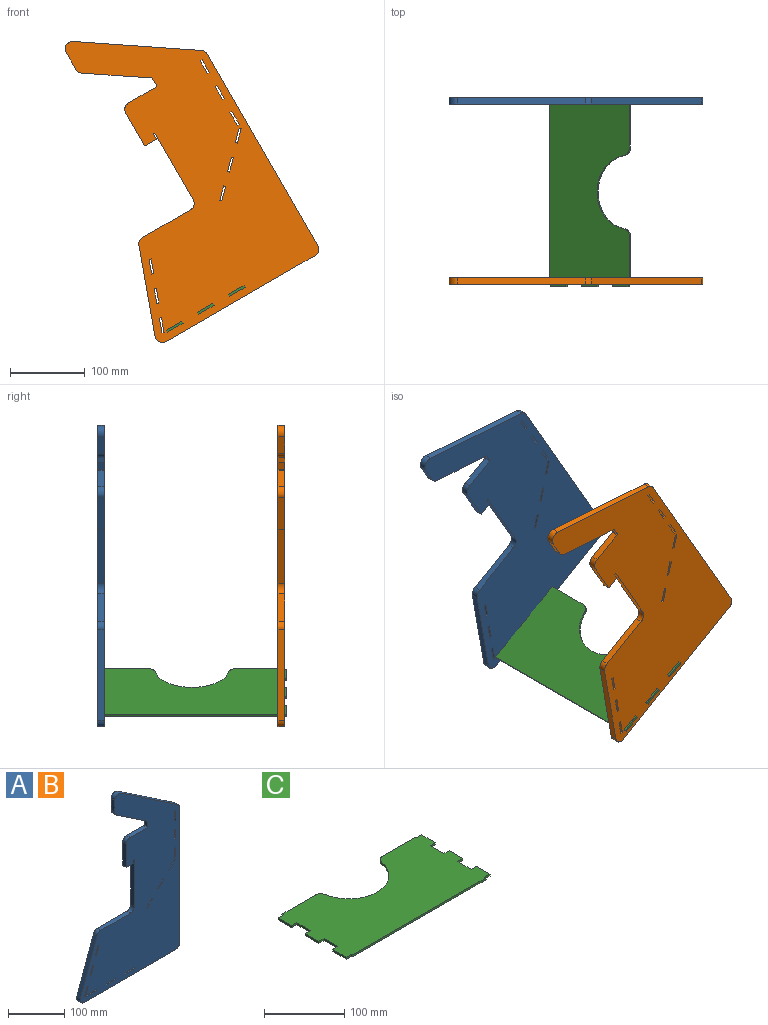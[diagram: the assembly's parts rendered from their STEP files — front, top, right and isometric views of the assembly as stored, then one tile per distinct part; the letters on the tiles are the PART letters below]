
ASSEMBLY  parts=3 mates=6
PART A: 77 faces, bbox 250.5x9x412.1 mm
  f0: plane 9x2.73mm, normal (-0.34,0,-0.94), area 26.1mm2, adj f1,f74,f75,f76
  f1: plane 18.79x9mm, normal (-0.94,0,0.34), area 180mm2, adj f0,f2,f75,f76
  f2: plane 9x2.73mm, normal (0.34,0,0.94), area 26.1mm2, adj f1,f74,f75,f76
  f3: plane 9x2.9mm, normal (1,0,0), area 26.1mm2, adj f4,f62,f75,f76
  f4: plane 24x9mm, normal (0,0,-1), area 216mm2, adj f3,f5,f75,f76
  f5: plane 9x2.9mm, normal (-1,0,0), area 26.1mm2, adj f4,f62,f75,f76
  f6: plane 9x2.9mm, normal (1,0,0), area 26.1mm2, adj f7,f63,f75,f76
  f7: plane 24x9mm, normal (0,0,-1), area 216mm2, adj f6,f8,f75,f76
  f8: plane 9x2.9mm, normal (-1,0,0), area 26.1mm2, adj f7,f63,f75,f76
  f9: plane 14.14x14.14mm, normal (0.71,0,-0.71), area 180mm2, adj f10,f64,f75,f76
  f10: plane 9x2.05mm, normal (-0.71,0,-0.71), area 26.1mm2, adj f9,f11,f75,f76
  f11: plane 14.14x14.14mm, normal (-0.71,0,0.71), area 180mm2, adj f10,f64,f75,f76
  f12: plane 9x2.9mm, normal (0,0,1), area 26.1mm2, adj f13,f65,f75,f76
  f13: plane 20x9mm, normal (1,0,0), area 180mm2, adj f12,f14,f75,f76
  f14: plane 9x2.9mm, normal (0,0,-1), area 26.1mm2, adj f13,f65,f75,f76
  f15: plane 9x2.9mm, normal (0,0,1), area 26.1mm2, adj f16,f66,f75,f76
  f16: plane 20x9mm, normal (1,0,0), area 180mm2, adj f15,f17,f75,f76
  f17: plane 9x2.9mm, normal (0,0,-1), area 26.1mm2, adj f16,f66,f75,f76
  f18: plane 16x9mm, normal (0,0,-1), area 144mm2, adj f19,f67,f75,f76
  f19: cylinder r=1mm len=9mm, axis (0,1,0), area 14.1mm2, adj f18,f20,f75,f76
  f20: plane 9x7mm, normal (1,0,0), area 63mm2, adj f19,f21,f75,f76
  f21: cylinder r=1mm len=9mm, axis (0,1,0), area 14.1mm2, adj f20,f22,f75,f76
  f22: plane 9x0.2mm, normal (0,0,-1), area 1.8mm2, adj f21,f23,f75,f76
  f23: cylinder r=1mm len=9mm, axis (0,1,0), area 14.1mm2, adj f22,f24,f75,f76
  f24: plane 102.54x9mm, normal (-1,0,0), area 922.9mm2, adj f23,f25,f75,f76
  f25: cylinder r=10mm len=10mm, axis (0,1,0), area 141.4mm2, adj f24,f26,f75,f76
  f26: plane 74.11x9mm, normal (0,0,1), area 667mm2, adj f25,f27,f75,f76
  f27: cylinder r=10mm len=9.4mm, axis (0,1,0), area 110mm2, adj f26,f28,f75,f76
  f28: plane 116.47x42.39mm, normal (-0.94,0,0.34), area 1115.5mm2, adj f27,f29,f75,f76
  f29: cylinder r=10mm len=13.42mm, axis (0,1,0), area 172.8mm2, adj f28,f30,f75,f76
  f30: plane 230.5x9mm, normal (0,0,-1), area 2074.5mm2, adj f29,f31,f75,f76
  f31: cylinder r=10mm len=10mm, axis (0,1,0), area 141.4mm2, adj f30,f32,f75,f76
  f32: plane 295.73x9mm, normal (1,0,0), area 2661.6mm2, adj f31,f33,f75,f76
  f33: cylinder r=10mm len=9mm, axis (0,1,0), area 88mm2, adj f32,f34,f75,f76
  f34: plane 142.9x96.39mm, normal (0.56,0,0.83), area 1551.4mm2, adj f33,f35,f75,f76
  f35: cylinder r=10mm len=15.59mm, axis (0,1,0), area 194.8mm2, adj f34,f36,f75,f76
  f36: plane 25.88x9mm, normal (-1,0,0), area 232.9mm2, adj f35,f37,f75,f76
  f37: cylinder r=10mm len=9mm, axis (0,1,0), area 88mm2, adj f36,f38,f75,f76
  f38: plane 78.5x52.95mm, normal (-0.56,0,-0.83), area 852.1mm2, adj f37,f39,f75,f76
  f39: plane 12x9mm, normal (-1,0,0), area 108mm2, adj f38,f40,f75,f76
  f40: cylinder r=1mm len=9mm, axis (0,1,0), area 14.1mm2, adj f39,f41,f75,f76
  f41: plane 43.2x9mm, normal (0,0,1), area 388.8mm2, adj f40,f42,f75,f76
  f42: cylinder r=10mm len=10mm, axis (0,1,0), area 141.4mm2, adj f41,f43,f75,f76
  f43: plane 50x9mm, normal (-1,0,0), area 450mm2, adj f42,f67,f75,f76
  f44: plane 9x2.9mm, normal (0,0,1), area 26.1mm2, adj f45,f68,f75,f76
  f45: plane 20x9mm, normal (1,0,0), area 180mm2, adj f44,f46,f75,f76
  f46: plane 9x2.9mm, normal (0,0,-1), area 26.1mm2, adj f45,f68,f75,f76
  f47: plane 14.14x14.14mm, normal (0.71,0,-0.71), area 180mm2, adj f48,f69,f75,f76
  f48: plane 9x2.05mm, normal (-0.71,0,-0.71), area 26.1mm2, adj f47,f49,f75,f76
  f49: plane 14.14x14.14mm, normal (-0.71,0,0.71), area 180mm2, adj f48,f69,f75,f76
  f50: plane 14.14x14.14mm, normal (0.71,0,-0.71), area 180mm2, adj f51,f70,f75,f76
  f51: plane 9x2.05mm, normal (-0.71,0,-0.71), area 26.1mm2, adj f50,f52,f75,f76
  f52: plane 14.14x14.14mm, normal (-0.71,0,0.71), area 180mm2, adj f51,f70,f75,f76
  f53: plane 9x2.9mm, normal (1,0,0), area 26.1mm2, adj f54,f71,f75,f76
  f54: plane 24x9mm, normal (0,0,-1), area 216mm2, adj f53,f55,f75,f76
  f55: plane 9x2.9mm, normal (-1,0,0), area 26.1mm2, adj f54,f71,f75,f76
  f56: plane 18.79x9mm, normal (0.94,0,-0.34), area 180mm2, adj f57,f72,f75,f76
  f57: plane 9x2.73mm, normal (-0.34,0,-0.94), area 26.1mm2, adj f56,f58,f75,f76
  f58: plane 18.79x9mm, normal (-0.94,0,0.34), area 180mm2, adj f57,f72,f75,f76
  f59: plane 18.79x9mm, normal (0.94,0,-0.34), area 180mm2, adj f60,f73,f75,f76
  f60: plane 9x2.73mm, normal (-0.34,0,-0.94), area 26.1mm2, adj f59,f61,f75,f76
  f61: plane 18.79x9mm, normal (-0.94,0,0.34), area 180mm2, adj f60,f73,f75,f76
  f62: plane 24x9mm, normal (0,0,1), area 216mm2, adj f3,f5,f75,f76
  f63: plane 24x9mm, normal (0,0,1), area 216mm2, adj f6,f8,f75,f76
  f64: plane 9x2.05mm, normal (0.71,0,0.71), area 26.1mm2, adj f9,f11,f75,f76
  f65: plane 20x9mm, normal (-1,0,0), area 180mm2, adj f12,f14,f75,f76
  f66: plane 20x9mm, normal (-1,0,0), area 180mm2, adj f15,f17,f75,f76
  f67: cylinder r=1mm len=9mm, axis (0,1,0), area 14.1mm2, adj f18,f43,f75,f76
  f68: plane 20x9mm, normal (-1,0,0), area 180mm2, adj f44,f46,f75,f76
  f69: plane 9x2.05mm, normal (0.71,0,0.71), area 26.1mm2, adj f47,f49,f75,f76
  f70: plane 9x2.05mm, normal (0.71,0,0.71), area 26.1mm2, adj f50,f52,f75,f76
  f71: plane 24x9mm, normal (0,0,1), area 216mm2, adj f53,f55,f75,f76
  f72: plane 9x2.73mm, normal (0.34,0,0.94), area 26.1mm2, adj f56,f58,f75,f76
  f73: plane 9x2.73mm, normal (0.34,0,0.94), area 26.1mm2, adj f59,f61,f75,f76
  f74: plane 18.79x9mm, normal (0.94,0,-0.34), area 180mm2, adj f0,f2,f75,f76
  f75: plane 412.12x250.5mm, normal (0,-1,0), area 57595.4mm2, adj f0,f1,f2,f3,f4,f5,f6,f7
  f76: plane 412.12x250.5mm, normal (0,1,0), area 57595.4mm2, adj f0,f1,f2,f3,f4,f5,f6,f7
PART B: same geometry as A
PART C: 34 faces, bbox 253x124x3 mm
  f0: plane 9x3mm, normal (0,1,0), area 27mm2, adj f1,f31,f32,f33
  f1: plane 24x3mm, normal (-1,0,0), area 72mm2, adj f0,f2,f32,f33
  f2: plane 9x3mm, normal (0,-1,0), area 27mm2, adj f1,f3,f32,f33
  f3: plane 24x3mm, normal (-1,0,0), area 72mm2, adj f2,f4,f32,f33
  f4: plane 9x3mm, normal (0,1,0), area 27mm2, adj f3,f5,f32,f33
  f5: plane 24x3mm, normal (-1,0,0), area 72mm2, adj f4,f6,f32,f33
  f6: plane 9x3mm, normal (0,-1,0), area 27mm2, adj f5,f7,f32,f33
  f7: plane 24x3mm, normal (-1,0,0), area 72mm2, adj f6,f8,f32,f33
  f8: plane 9x3mm, normal (0,1,0), area 27mm2, adj f7,f9,f32,f33
  f9: plane 24x3mm, normal (-1,0,0), area 72mm2, adj f8,f10,f32,f33
  f10: plane 9x3mm, normal (0,-1,0), area 27mm2, adj f9,f11,f32,f33
  f11: plane 3x2mm, normal (-1,0,0), area 6mm2, adj f10,f12,f32,f33
  f12: plane 235x3mm, normal (0,-1,0), area 705mm2, adj f11,f13,f32,f33
  f13: plane 3x2mm, normal (1,0,0), area 6mm2, adj f12,f14,f32,f33
  f14: plane 9x3mm, normal (0,-1,0), area 27mm2, adj f13,f15,f32,f33
  f15: plane 24x3mm, normal (1,0,0), area 72mm2, adj f14,f16,f32,f33
  f16: plane 9x3mm, normal (0,1,0), area 27mm2, adj f15,f17,f32,f33
  f17: plane 24x3mm, normal (1,0,0), area 72mm2, adj f16,f18,f32,f33
  f18: plane 9x3mm, normal (0,-1,0), area 27mm2, adj f17,f19,f32,f33
  f19: plane 24x3mm, normal (1,0,0), area 72mm2, adj f18,f20,f32,f33
  f20: plane 9x3mm, normal (0,1,0), area 27mm2, adj f19,f21,f32,f33
  f21: plane 24x3mm, normal (1,0,0), area 72mm2, adj f20,f22,f32,f33
  f22: plane 9x3mm, normal (0,-1,0), area 27mm2, adj f21,f23,f32,f33
  f23: plane 24x3mm, normal (1,0,0), area 72mm2, adj f22,f24,f32,f33
  f24: plane 9x3mm, normal (0,1,0), area 27mm2, adj f23,f25,f32,f33
  f25: plane 3x2mm, normal (1,0,0), area 6mm2, adj f24,f26,f32,f33
  f26: plane 58.34x3mm, normal (0,1,0), area 175mm2, adj f25,f27,f32,f33
  f27: cylinder r=10mm len=9.86mm, axis (0,0,-1), area 42.1mm2, adj f26,f28,f32,f33
  f28: cylinder r=50mm len=98.6mm, axis (0,0,-1), area 421mm2, adj f27,f29,f32,f33
  f29: cylinder r=10mm len=9.86mm, axis (0,0,-1), area 42.1mm2, adj f28,f30,f32,f33
  f30: plane 58.34x3mm, normal (0,1,0), area 175mm2, adj f29,f31,f32,f33
  f31: plane 3x2mm, normal (-1,0,0), area 6mm2, adj f0,f30,f32,f33
  f32: plane 253x124mm, normal (0,0,1), area 26476.4mm2, adj f0,f1,f2,f3,f4,f5,f6,f7
  f33: plane 253x124mm, normal (0,0,-1), area 26476.4mm2, adj f0,f1,f2,f3,f4,f5,f6,f7
PLACE A rot(axis=(0,-1,0),30deg) t=(-262.21,-45.28,234.12)mm
PLACE B rot(axis=(0,-1,0),30deg) t=(-262.21,-286.88,234.12)mm
PLACE C rot(axis=(0.25,-0.25,-0.94),93.8deg) t=(-136.08,-171.78,-45.36)mm
MATE planar C.f10 <-> A.f53  axis (-0.87,0,-0.5) through (-242.48,-49.78,-105.06)mm
MATE parallel A.f75 <-> B.f75  axis (0,-1,0) through (-193.32,-54.28,87.84)mm
MATE planar C.f32 <-> A.f54  axis (-0.5,0,0.87) through (-196.57,-171.78,-76.83)mm
MATE planar B.f54 <-> C.f32  axis (0.5,0,-0.87) through (-232.84,-291.38,-97.77)mm
MATE planar C.f14 <-> B.f53  axis (-0.87,0,-0.5) through (-242.48,-293.78,-105.06)mm
MATE planar A.f76 <-> C.f1  axis (0,1,0) through (-193.32,-45.28,87.84)mm
